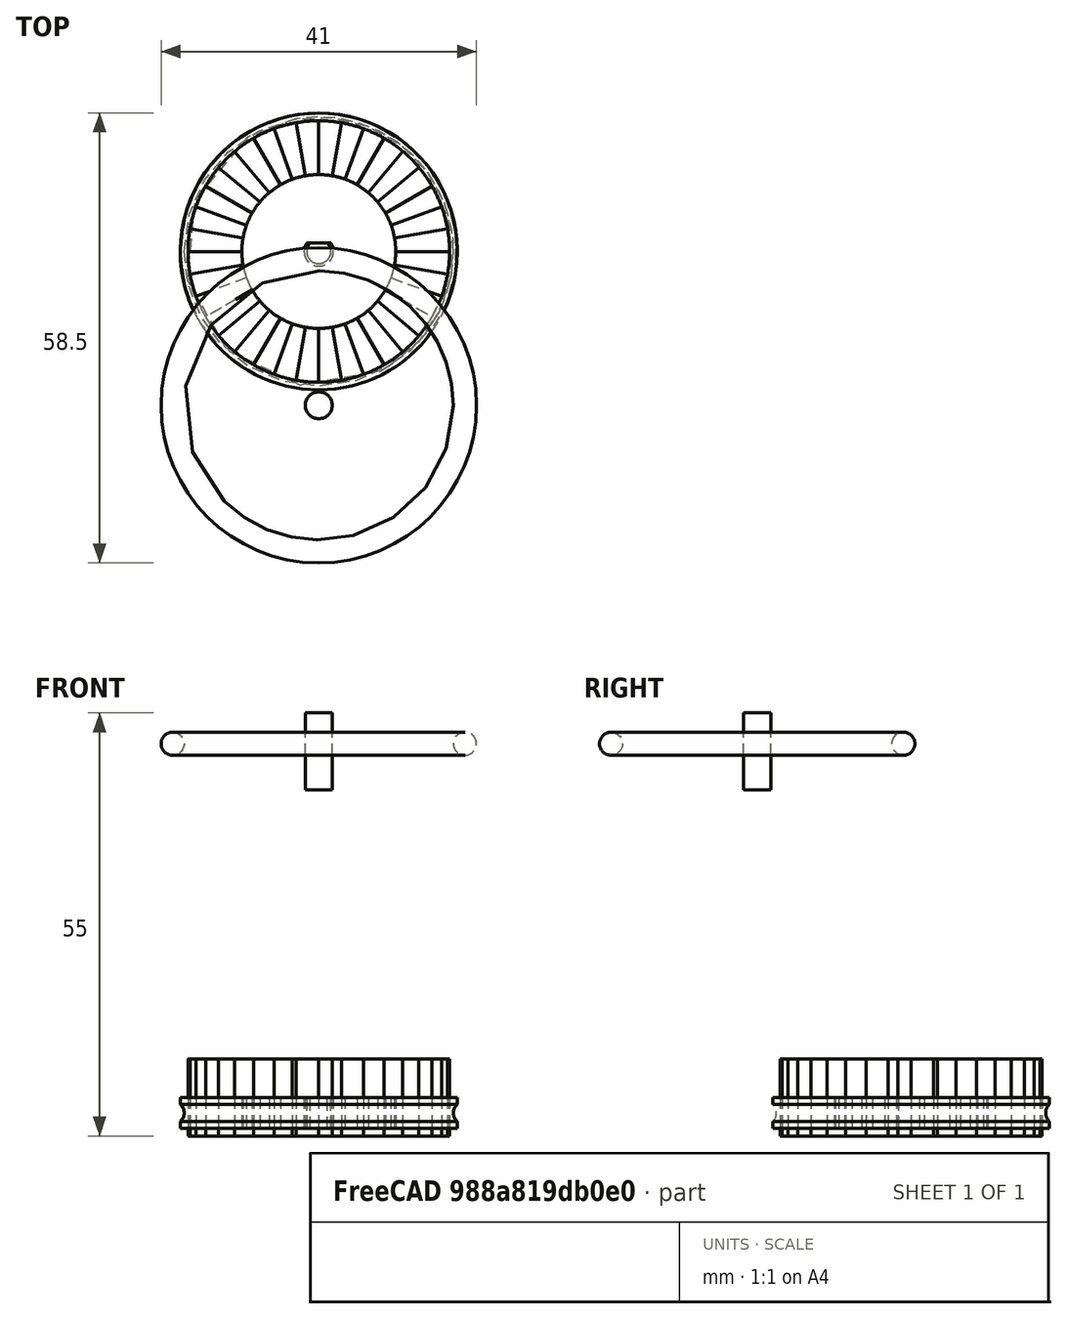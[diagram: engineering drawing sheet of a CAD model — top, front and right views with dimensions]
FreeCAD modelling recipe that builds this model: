
FCSTD DOCUMENT  (FreeCAD 0.18.4R)
Label: Wheel 0.1
License: All rights reserved
LicenseURL: http://en.wikipedia.org/wiki/All_rights_reserved
objects: Part::Feature×35, Part::Cut×12, Part::Cylinder×7, Part::Box×5, Part::Torus×3, Part::MultiFuse×2
note: 64 computed .brp shape members not serialized (recipe doc carries the construction recipe); baked Part::Feature solids carry a one-line shape summary decoded from their .brp

FEATURE [Part::Cylinder] Cylinder012  label="wheel1a"
  Angle = 360
  AttacherType = Attacher::AttachEngine3D
  Height = 4
  Radius = 18
FEATURE [Part::Cylinder] Cylinder028  label="Cylinder024"
  Angle = 360
  AttacherType = Attacher::AttachEngine3D
  Height = 10
  Placement = pos=(0,0,-1) rot=(0,0,1;0rad)
  Radius = 1.57
FEATURE [Part::Box] Box084016  label="Cube067"
  AttacherType = Attacher::AttachEngine3D
  Height = 12
  Length = 10
  Placement = pos=(-5,1.1,-1.5) rot=(0,0,1;0rad)
  Width = 10
FEATURE [Part::Cut] Cut057
  Base = -> Cylinder028
  Tool = -> Box084016
FEATURE [Part::Cut] Cut062
  Base = -> Cylinder012
  Tool = -> Cut057
FEATURE [Part::Torus] Torus002
  Angle1 = -180
  Angle2 = 180
  Angle3 = 360
  AttacherType = Attacher::AttachEngine3D
  Placement = pos=(0,0,2) rot=(0,0,1;0rad)
  Radius1 = 19
  Radius2 = 1.5
FEATURE [Part::Cut] Cut063  label="wheel 0.1"
  Base = -> Cut062
  Tool = -> Torus002
FEATURE [Part::Torus] Torus
  Angle1 = -180
  Angle2 = 180
  Angle3 = 360
  AttacherType = Attacher::AttachEngine3D
  Placement = pos=(0,-20,50) rot=(0,0,1;0rad)
  Radius1 = 19
  Radius2 = 1.5
FEATURE [Part::Cylinder] Cylinder062  label="Cylinder158"
  Angle = 360
  AttacherType = Attacher::AttachEngine3D
  Height = 10
  Radius = 17
FEATURE [Part::Cylinder] Cylinder063  label="Cylinder159"
  Angle = 360
  AttacherType = Attacher::AttachEngine3D
  Height = 16
  Placement = pos=(0,0,-4) rot=(0,0,1;0rad)
  Radius = 10
FEATURE [Part::Cut] Cut044
  Base = -> Cylinder062
  Tool = -> Cylinder063
FEATURE [Part::Box] Box026  label="Cube025"
  AttacherType = Attacher::AttachEngine3D
  Height = 20
  Length = 18
  Placement = pos=(0,0,-5) rot=(0,0,1;0rad)
  Width = 20
FEATURE [Part::Box] Box027  label="Cube026"
  AttacherType = Attacher::AttachEngine3D
  Height = 20
  Length = 10
  Placement = pos=(0,0,-5) rot=(0,0,1;0.174533rad)
  Width = 20
FEATURE [Part::Cut] Cut045
  Base = -> Box027
  Tool = -> Box026
FEATURE [Part::Feature] Cut045001
  Placement = pos=(0,0,0) rot=(0,0,1;0.349066rad)
  shape: bbox 10 x 22.32 x 20 mm, 7 faces (baked)
FEATURE [Part::Feature] Cut045002
  Placement = pos=(0,0,0) rot=(0,0,1;0.698132rad)
  shape: bbox 15.32 x 20.52 x 20 mm, 7 faces (baked)
FEATURE [Part::Feature] Cut045003
  Placement = pos=(0,0,0) rot=(0,0,1;1.0472rad)
  shape: bbox 18.79 x 16.24 x 20 mm, 7 faces (baked)
FEATURE [Part::Feature] Cut045004
  Placement = pos=(0,0,0) rot=(0,0,1;1.39626rad)
  shape: bbox 20 x 10 x 20 mm, 7 faces (baked)
FEATURE [Part::Feature] Cut045005
  Placement = pos=(0,0,0) rot=(0,0,1;1.74533rad)
  shape: bbox 22.21 x 9.894 x 20 mm, 7 faces (baked)
FEATURE [Part::Feature] Cut045006
  Placement = pos=(0,0,0) rot=(0,0,1;2.0944rad)
  shape: bbox 21.75 x 12.86 x 20 mm, 7 faces (baked)
FEATURE [Part::Feature] Cut045007
  Placement = pos=(0,0,0) rot=(0,0,1;2.44346rad)
  shape: bbox 18.66 x 17.32 x 20 mm, 7 faces (baked)
FEATURE [Part::Feature] Cut045008
  Placement = pos=(0,0,0) rot=(0,0,1;2.79253rad)
  shape: bbox 13.32 x 19.7 x 20 mm, 7 faces (baked)
FEATURE [Part::Feature] Cut045009
  Placement = pos=(0,0,0) rot=(0,0,1;3.14159rad)
  shape: bbox 10.1 x 21.43 x 20 mm, 7 faces (baked)
FEATURE [Part::Feature] Cut045010
  Placement = pos=(0,0,0) rot=(0,0,1;3.49066rad)
  shape: bbox 10 x 22.32 x 20 mm, 7 faces (baked)
FEATURE [Part::Feature] Cut045011
  Placement = pos=(0,0,0) rot=(0,0,1;3.83972rad)
  shape: bbox 15.32 x 20.52 x 20 mm, 7 faces (baked)
FEATURE [Part::Feature] Cut045012
  Placement = pos=(0,0,0) rot=(0,0,1;4.18879rad)
  shape: bbox 18.79 x 16.24 x 20 mm, 7 faces (baked)
FEATURE [Part::Feature] Cut045013
  Placement = pos=(0,0,0) rot=(0,0,-1;1.74533rad)
  shape: bbox 20 x 10 x 20 mm, 7 faces (baked)
FEATURE [Part::Feature] Cut045014
  Placement = pos=(0,0,0) rot=(0,0,-1;1.39626rad)
  shape: bbox 22.21 x 9.894 x 20 mm, 7 faces (baked)
FEATURE [Part::Feature] Cut045015
  Placement = pos=(0,0,0) rot=(0,0,-1;1.0472rad)
  shape: bbox 21.75 x 12.86 x 20 mm, 7 faces (baked)
FEATURE [Part::Feature] Cut045016
  Placement = pos=(0,0,0) rot=(0,0,-1;0.698132rad)
  shape: bbox 18.66 x 17.32 x 20 mm, 7 faces (baked)
FEATURE [Part::Feature] Cut045017
  Placement = pos=(0,0,0) rot=(0,0,-1;0.349066rad)
  shape: bbox 13.32 x 19.7 x 20 mm, 7 faces (baked)
FEATURE [Part::MultiFuse] Fusion095
  Shapes = -> [Cut045001,Cut045008,Cut045010,Cut045009,Cut045005,Cut045003,Cut045006,Cut045002,Cut045004,Cut045007,Cut045016,Cut045017,Cut045011,Cut045012,Cut045013,Cut045014,Cut045015,Cut045]
FEATURE [Part::Cut] Cut045018
  Base = -> Cut044
  Placement = pos=(0,0,-1) rot=(0,1,0;0rad)
  Tool = -> Fusion095
FEATURE [Part::Cylinder] Cylinder064  label="Cylinder160"
  Angle = 360
  AttacherType = Attacher::AttachEngine3D
  Height = 10
  Placement = pos=(0,-20,44) rot=(0,0,1;0rad)
  Radius = 1.75
FEATURE [Part::Cut] Cut008
FEATURE [Part::Torus] Torus001
  Angle1 = -180
  Angle2 = 180
  Angle3 = 360
  AttacherType = Attacher::AttachEngine3D
  Placement = pos=(0,0,2) rot=(0,0,1;0rad)
  Radius1 = 19
  Radius2 = 1.5
FEATURE [Part::Cut] Cut009  label="wheel2"
  Base = -> Cut008
  Placement = pos=(75,-7,15) rot=(0,1,0;1.5708rad)
  Tool = -> Torus001
FEATURE [Part::Cylinder] Cylinder065  label="Cylinder161"
  Angle = 360
  AttacherType = Attacher::AttachEngine3D
  Height = 10
  Radius = 17
FEATURE [Part::Cylinder] Cylinder066  label="Cylinder162"
  Angle = 360
  AttacherType = Attacher::AttachEngine3D
  Height = 16
  Placement = pos=(0,0,-4) rot=(0,0,1;0rad)
  Radius = 10
FEATURE [Part::Cut] Cut045019
  Base = -> Cylinder065
  Tool = -> Cylinder066
FEATURE [Part::Box] Box084017  label="Cube068"
  AttacherType = Attacher::AttachEngine3D
  Height = 20
  Length = 18
  Placement = pos=(0,0,-5) rot=(0,0,1;0rad)
  Width = 20
FEATURE [Part::Box] Box084018  label="Cube069"
  AttacherType = Attacher::AttachEngine3D
  Height = 20
  Length = 10
  Placement = pos=(0,0,-5) rot=(0,0,1;0.174533rad)
  Width = 20
FEATURE [Part::Cut] Cut045020
  Base = -> Box084018
  Tool = -> Box084017
FEATURE [Part::Feature] Cut045021
  Placement = pos=(0,0,0) rot=(0,0,1;0.349066rad)
  shape: bbox 10 x 22.32 x 20 mm, 7 faces (baked)
FEATURE [Part::Feature] Cut045022
  Placement = pos=(0,0,0) rot=(0,0,1;0.698132rad)
  shape: bbox 15.32 x 20.52 x 20 mm, 7 faces (baked)
FEATURE [Part::Feature] Cut045023
  Placement = pos=(0,0,0) rot=(0,0,1;1.0472rad)
  shape: bbox 18.79 x 16.24 x 20 mm, 7 faces (baked)
FEATURE [Part::Feature] Cut045024
  Placement = pos=(0,0,0) rot=(0,0,1;1.39626rad)
  shape: bbox 20 x 10 x 20 mm, 7 faces (baked)
FEATURE [Part::Feature] Cut045025
  Placement = pos=(0,0,0) rot=(0,0,1;1.74533rad)
  shape: bbox 22.21 x 9.894 x 20 mm, 7 faces (baked)
FEATURE [Part::Feature] Cut045026
  Placement = pos=(0,0,0) rot=(0,0,1;2.0944rad)
  shape: bbox 21.75 x 12.86 x 20 mm, 7 faces (baked)
FEATURE [Part::Feature] Cut045027
  Placement = pos=(0,0,0) rot=(0,0,1;2.44346rad)
  shape: bbox 18.66 x 17.32 x 20 mm, 7 faces (baked)
FEATURE [Part::Feature] Cut045028
  Placement = pos=(0,0,0) rot=(0,0,1;2.79253rad)
  shape: bbox 13.32 x 19.7 x 20 mm, 7 faces (baked)
FEATURE [Part::Feature] Cut045029
  Placement = pos=(0,0,0) rot=(0,0,1;3.14159rad)
  shape: bbox 10.1 x 21.43 x 20 mm, 7 faces (baked)
FEATURE [Part::Feature] Cut045030
  Placement = pos=(0,0,0) rot=(0,0,1;3.49066rad)
  shape: bbox 10 x 22.32 x 20 mm, 7 faces (baked)
FEATURE [Part::Feature] Cut045031
  Placement = pos=(0,0,0) rot=(0,0,1;3.83972rad)
  shape: bbox 15.32 x 20.52 x 20 mm, 7 faces (baked)
FEATURE [Part::Feature] Cut045032
  Placement = pos=(0,0,0) rot=(0,0,1;4.18879rad)
  shape: bbox 18.79 x 16.24 x 20 mm, 7 faces (baked)
FEATURE [Part::Feature] Cut045033
  Placement = pos=(0,0,0) rot=(0,0,-1;1.74533rad)
  shape: bbox 20 x 10 x 20 mm, 7 faces (baked)
FEATURE [Part::Feature] Cut045034
  Placement = pos=(0,0,0) rot=(0,0,-1;1.39626rad)
  shape: bbox 22.21 x 9.894 x 20 mm, 7 faces (baked)
FEATURE [Part::Feature] Cut045035
  Placement = pos=(0,0,0) rot=(0,0,-1;1.0472rad)
  shape: bbox 21.75 x 12.86 x 20 mm, 7 faces (baked)
FEATURE [Part::Feature] Cut045036
  Placement = pos=(0,0,0) rot=(0,0,-1;0.698132rad)
  shape: bbox 18.66 x 17.32 x 20 mm, 7 faces (baked)
FEATURE [Part::Feature] Cut045037
  Placement = pos=(0,0,0) rot=(0,0,-1;0.349066rad)
  shape: bbox 13.32 x 19.7 x 20 mm, 7 faces (baked)
FEATURE [Part::MultiFuse] Fusion096
  Shapes = -> [Cut045021,Cut045028,Cut045030,Cut045029,Cut045025,Cut045023,Cut045026,Cut045022,Cut045024,Cut045027,Cut045036,Cut045037,Cut045031,Cut045032,Cut045033,Cut045034,Cut045035,Cut045020]
FEATURE [Part::Cut] Cut045038
  Base = -> Cut045019
  Placement = pos=(72,-7,15) rot=(0,1,0;1.5708rad)
  Tool = -> Fusion096
FEATURE [Part::Cut] Cut045039  label="Wheel with Spokes AB"
  Base = -> Cut009
  Placement = pos=(-15,7,79) rot=(0,1,0;1.5708rad)
  Tool = -> Cut045038
FEATURE [Part::Feature] Cut063_cs
  shape: bbox 35 x 35 x 3e-07 mm, 0 faces, 0 solids (baked)
